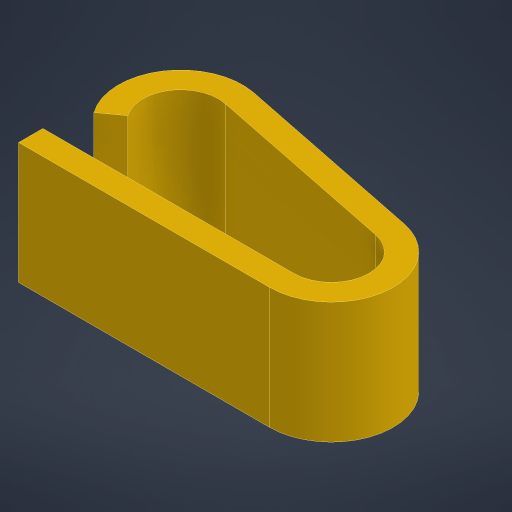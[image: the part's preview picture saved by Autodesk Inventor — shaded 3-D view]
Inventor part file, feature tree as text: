
AUTODESK INVENTOR PART (.ipt)
format: ipt  version: 2024.3 (Build 283343010, 343A)  size: 169,472 bytes
history: native  units: mm
features: extrude x1, sketch x1
ambient origin geometry x8: Origin, YZ Plane, XZ Plane, XY Plane, X Axis, Y Axis, Z Axis, Center Point
bodies: Volumenkörper1 (feature_tree)
feature tree (2):
  extrude  "Extrusion1"  Depth=1.0mm
  sketch  "Skizze1"  dims[d0=0.2mm d1=1.1mm d2=2.5mm d3=1.0mm d4=0.0mm]
